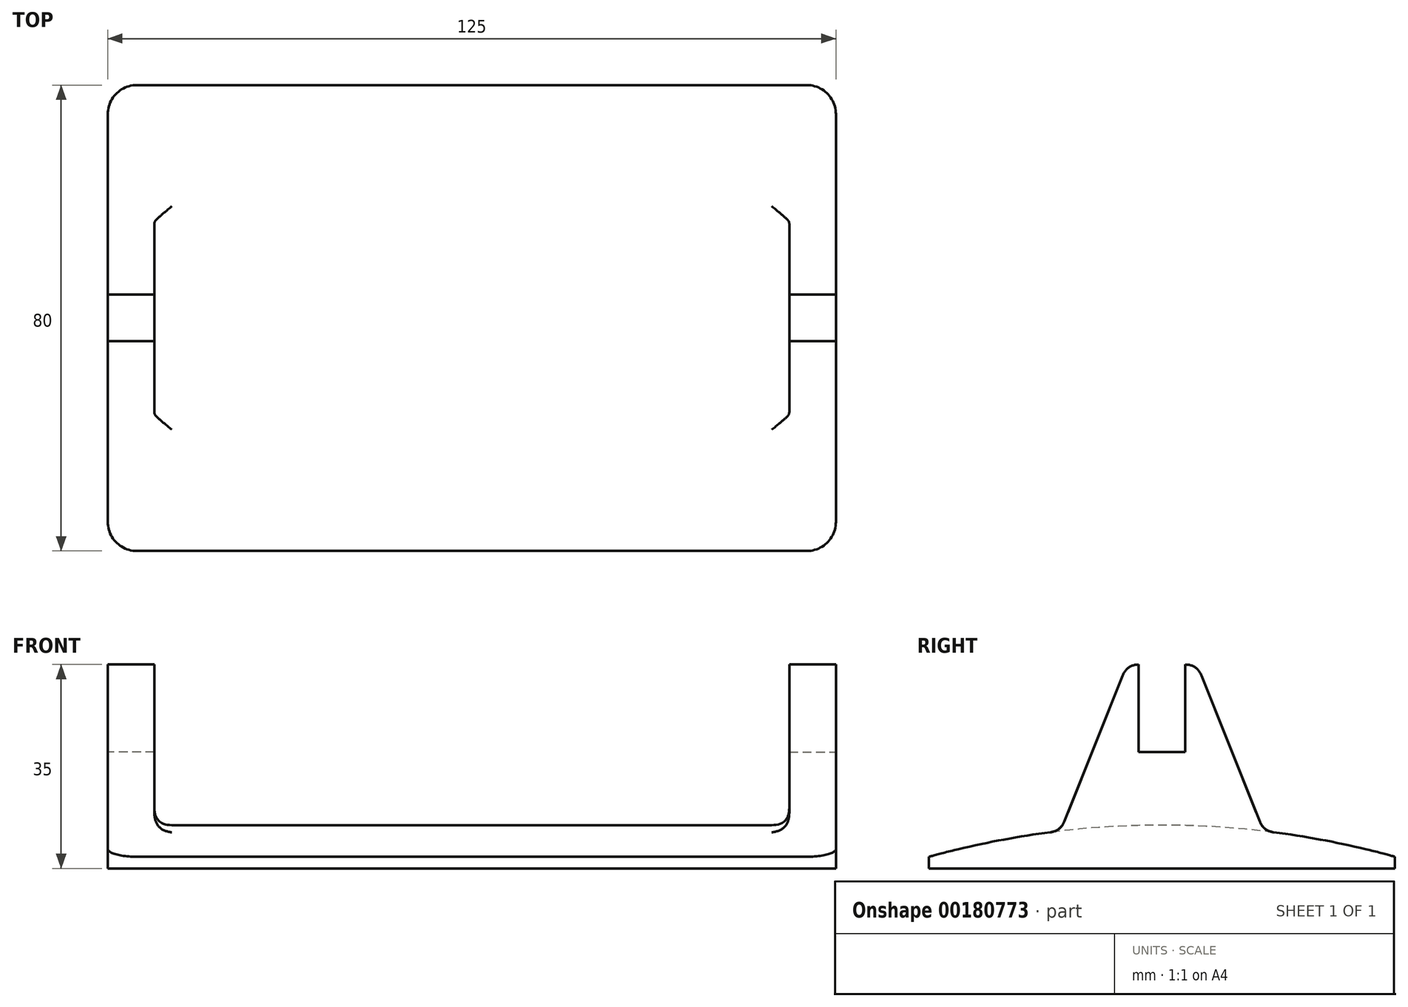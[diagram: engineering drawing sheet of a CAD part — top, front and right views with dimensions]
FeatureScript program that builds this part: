
annotation { "Feature Type Name" : "Feature", "Feature Type Description" : "" }
export const myFeature = defineFeature(function(context is Context, id is Id, definition is map)
    precondition{}
    {
        {
            var Q0;
            Q0=qCreatedBy(makeId("Right.planeOp"),FACE);
            var sketch = newSketch(context, id + "F0", { "sketchPlane" : qUnion([Q0])});
            skLineSegment(sketch, "E0", {"start": v(-40, 0) * mm, "end": v(40, 0) * mm});
            skLineSegment(sketch, "E1", {"start": v(40, 0) * mm, "end": v(40, 2) * mm});
            skLineSegment(sketch, "E2", {"start": v(-40, 0) * mm, "end": v(-40, 2) * mm});
            skArc(sketch, "E3", {"start": v(40, 2) * mm, "mid": v(0, 7.43) * mm, "end": v(-40, 2) * mm});
            skSolve(sketch);
        }
        {
            var Q0;
            Q0 = qSketchRegion(id + "F0", true);
            extrude(context, id + "F1", {"entities" : qUnion([Q0]), "endBound" : BoundingType.SYMMETRIC, "depth" : 125 * mm});
        }
        {
            var Q0;
            Q0=makeQuery(id+"F1.opExtrude","CAP_FACE",FACE,{"disambiguationData":[OSD([sQuery(id+"F0.wireOp",EDGE,"E0"),sQuery(id+"F0.wireOp",EDGE,"E1"),sQuery(id+"F0.wireOp",EDGE,"E2"),sQuery(id+"F0.wireOp",EDGE,"E3")])],"isStart":false});
            var sketch = newSketch(context, id + "F2", { "sketchPlane" : qUnion([Q0])});
            skLineSegment(sketch, "E4", {"start": v(-20, 0) * mm, "end": v(-6, 35) * mm});
            skLineSegment(sketch, "E5", {"start": v(-6, 35) * mm, "end": v(-4, 35) * mm});
            skLineSegment(sketch, "E6", {"start": v(-4, 35) * mm, "end": v(-4, 20) * mm});
            skLineSegment(sketch, "E7", {"start": v(-4, 20) * mm, "end": v(4, 20) * mm});
            skLineSegment(sketch, "E8", {"start": v(4, 20) * mm, "end": v(4, 35) * mm});
            skLineSegment(sketch, "E9", {"start": v(4, 35) * mm, "end": v(6, 35) * mm});
            skLineSegment(sketch, "E10", {"start": v(6, 35) * mm, "end": v(20, 0) * mm});
            skLineSegment(sketch, "E11", {"start": v(20, 0) * mm, "end": v(-20, 0) * mm});
            skSolve(sketch);
        }
        {
            var Q0;
            Q0 = qSketchRegion(id + "FxaWVvKuadnkObY_1", true);
            var Q1;
            Q1 = qSketchRegion(id + "F2", true);
            extrude(context, id + "F3", {"entities" : qUnion([Q0, Q1]), "oppositeDirection" : true, "depth" : 8 * mm});
        }
        {
            var Q0;
            Q0=makeQuery(id+"F3.opExtrude","SWEPT_BODY",BODY,{"disambiguationData":[OSD([sQuery(id+"F2.wireOp",EDGE,"E4"),sQuery(id+"F2.wireOp",EDGE,"E5"),sQuery(id+"F2.wireOp",EDGE,"E6"),sQuery(id+"F2.wireOp",EDGE,"E7"),sQuery(id+"F2.wireOp",EDGE,"E8"),sQuery(id+"F2.wireOp",EDGE,"E9"),sQuery(id+"F2.wireOp",EDGE,"E10"),sQuery(id+"F2.wireOp",EDGE,"E11")])]});
            var Q1;
            Q1=qCreatedBy(makeId("Right.planeOp"),FACE);
            mirror(context, id + "F4", {"operationType" : NewBodyOperationType.ADD, "entities" : qUnion([Q0]), "mirrorPlane" : qUnion([Q1])});
        }
        {
            var Q0;
            Q0=makeQuery(id+"F4.boolean.opBoolean","INTERSECT",EDGE,{"derivedFrom":[makeQuery(id+"F1.opExtrude","SWEPT_FACE",FACE,{"disambiguationData":[OSD([sQuery(id+"F0.wireOp",EDGE,"E3")])]}),makeQuery(id+"F3.opExtrude","SWEPT_FACE",FACE,{"disambiguationData":[OSD([sQuery(id+"F2.wireOp",EDGE,"E4")])]})]});
            var Q1;
            Q1=makeQuery(id+"F3.opExtrude","SWEPT_EDGE",EDGE,{"disambiguationData":[OSD([sQuery(id+"F2.wireOp",EDGE,"E4"),sQuery(id+"F2.wireOp",EDGE,"E5")])]});
            var Q2;
            Q2=makeQuery(id+"F3.opExtrude","SWEPT_EDGE",EDGE,{"disambiguationData":[OSD([sQuery(id+"F2.wireOp",EDGE,"E9"),sQuery(id+"F2.wireOp",EDGE,"E10")])]});
            var Q3;
            Q3=makeQuery(id+"F4.boolean.opBoolean","INTERSECT",EDGE,{"derivedFrom":[makeQuery(id+"F1.opExtrude","SWEPT_FACE",FACE,{"disambiguationData":[OSD([sQuery(id+"F0.wireOp",EDGE,"E3")])]}),makeQuery(id+"F3.opExtrude","SWEPT_FACE",FACE,{"disambiguationData":[OSD([sQuery(id+"F2.wireOp",EDGE,"E10")])]})]});
            var Q4;
            Q4=makeQuery(id+"F4.opPattern","COPY",EDGE,{"derivedFrom":makeQuery(id+"F3.opExtrude","SWEPT_EDGE",EDGE,{"disambiguationData":[OSD([sQuery(id+"F2.wireOp",EDGE,"E4"),sQuery(id+"F2.wireOp",EDGE,"E5")])]}),"instanceName":"1"});
            var Q5;
            Q5=makeQuery(id+"F4.boolean.opBoolean","INTERSECT",EDGE,{"derivedFrom":[makeQuery(id+"F1.opExtrude","SWEPT_FACE",FACE,{"disambiguationData":[OSD([sQuery(id+"F0.wireOp",EDGE,"E3")])]}),makeQuery(id+"F4.opPattern","COPY",FACE,{"derivedFrom":makeQuery(id+"F3.opExtrude","SWEPT_FACE",FACE,{"disambiguationData":[OSD([sQuery(id+"F2.wireOp",EDGE,"E4")])]}),"instanceName":"1"})]});
            var Q6;
            Q6=makeQuery(id+"F4.opPattern","COPY",EDGE,{"derivedFrom":makeQuery(id+"F3.opExtrude","SWEPT_EDGE",EDGE,{"disambiguationData":[OSD([sQuery(id+"F2.wireOp",EDGE,"E9"),sQuery(id+"F2.wireOp",EDGE,"E10")])]}),"instanceName":"1"});
            var Q7;
            Q7=makeQuery(id+"F4.boolean.opBoolean","INTERSECT",EDGE,{"derivedFrom":[makeQuery(id+"F1.opExtrude","SWEPT_FACE",FACE,{"disambiguationData":[OSD([sQuery(id+"F0.wireOp",EDGE,"E3")])]}),makeQuery(id+"F4.opPattern","COPY",FACE,{"derivedFrom":makeQuery(id+"F3.opExtrude","SWEPT_FACE",FACE,{"disambiguationData":[OSD([sQuery(id+"F2.wireOp",EDGE,"E10")])]}),"instanceName":"1"})]});
            var Q8;
            Q8=makeQuery(id+"F4.boolean.opBoolean","INTERSECT",EDGE,{"derivedFrom":[makeQuery(id+"F1.opExtrude","SWEPT_FACE",FACE,{"disambiguationData":[OSD([sQuery(id+"F0.wireOp",EDGE,"E3")])]}),makeQuery(id+"F4.opPattern","COPY",FACE,{"derivedFrom":makeQuery(id+"F3.opExtrude","CAP_FACE",FACE,{"disambiguationData":[OSD([sQuery(id+"F2.wireOp",EDGE,"E4"),sQuery(id+"F2.wireOp",EDGE,"E5"),sQuery(id+"F2.wireOp",EDGE,"E6"),sQuery(id+"F2.wireOp",EDGE,"E7"),sQuery(id+"F2.wireOp",EDGE,"E8"),sQuery(id+"F2.wireOp",EDGE,"E9"),sQuery(id+"F2.wireOp",EDGE,"E10"),sQuery(id+"F2.wireOp",EDGE,"E11")])],"isStart":false}),"instanceName":"1"})]});
            var Q9;
            Q9=makeQuery(id+"F4.boolean.opBoolean","INTERSECT",EDGE,{"derivedFrom":[makeQuery(id+"F1.opExtrude","SWEPT_FACE",FACE,{"disambiguationData":[OSD([sQuery(id+"F0.wireOp",EDGE,"E3")])]}),makeQuery(id+"F3.opExtrude","CAP_FACE",FACE,{"disambiguationData":[OSD([sQuery(id+"F2.wireOp",EDGE,"E4"),sQuery(id+"F2.wireOp",EDGE,"E5"),sQuery(id+"F2.wireOp",EDGE,"E6"),sQuery(id+"F2.wireOp",EDGE,"E7"),sQuery(id+"F2.wireOp",EDGE,"E8"),sQuery(id+"F2.wireOp",EDGE,"E9"),sQuery(id+"F2.wireOp",EDGE,"E10"),sQuery(id+"F2.wireOp",EDGE,"E11")])],"isStart":false})]});
            fillet(context, id + "F5", {"entities" : qUnion([Q0, Q1, Q2, Q3, Q4, Q5, Q6, Q7, Q8, Q9]), "radius" : 3 * mm, "tangentPropagation" : true, "rho" : 0.5, "crossSection" : FilletCrossSection.CONIC, "allowEdgeOverflow" : false});
        }
        {
            var Q0;
            Q0=makeQuery(id+"F1.opExtrude","CAP_EDGE",EDGE,{"disambiguationData":[OSD([sQuery(id+"F0.wireOp",EDGE,"E2")])],"isStart":true});
            var Q1;
            Q1=makeQuery(id+"F1.opExtrude","CAP_EDGE",EDGE,{"disambiguationData":[OSD([sQuery(id+"F0.wireOp",EDGE,"E2")])],"isStart":false});
            var Q2;
            Q2=makeQuery(id+"F1.opExtrude","CAP_EDGE",EDGE,{"disambiguationData":[OSD([sQuery(id+"F0.wireOp",EDGE,"E1")])],"isStart":false});
            var Q3;
            Q3=makeQuery(id+"F1.opExtrude","CAP_EDGE",EDGE,{"disambiguationData":[OSD([sQuery(id+"F0.wireOp",EDGE,"E1")])],"isStart":true});
            fillet(context, id + "F6", {"entities" : qUnion([Q0, Q1, Q2, Q3]), "radius" : 5 * mm, "tangentPropagation" : true, "allowEdgeOverflow" : false});
        }
    });
